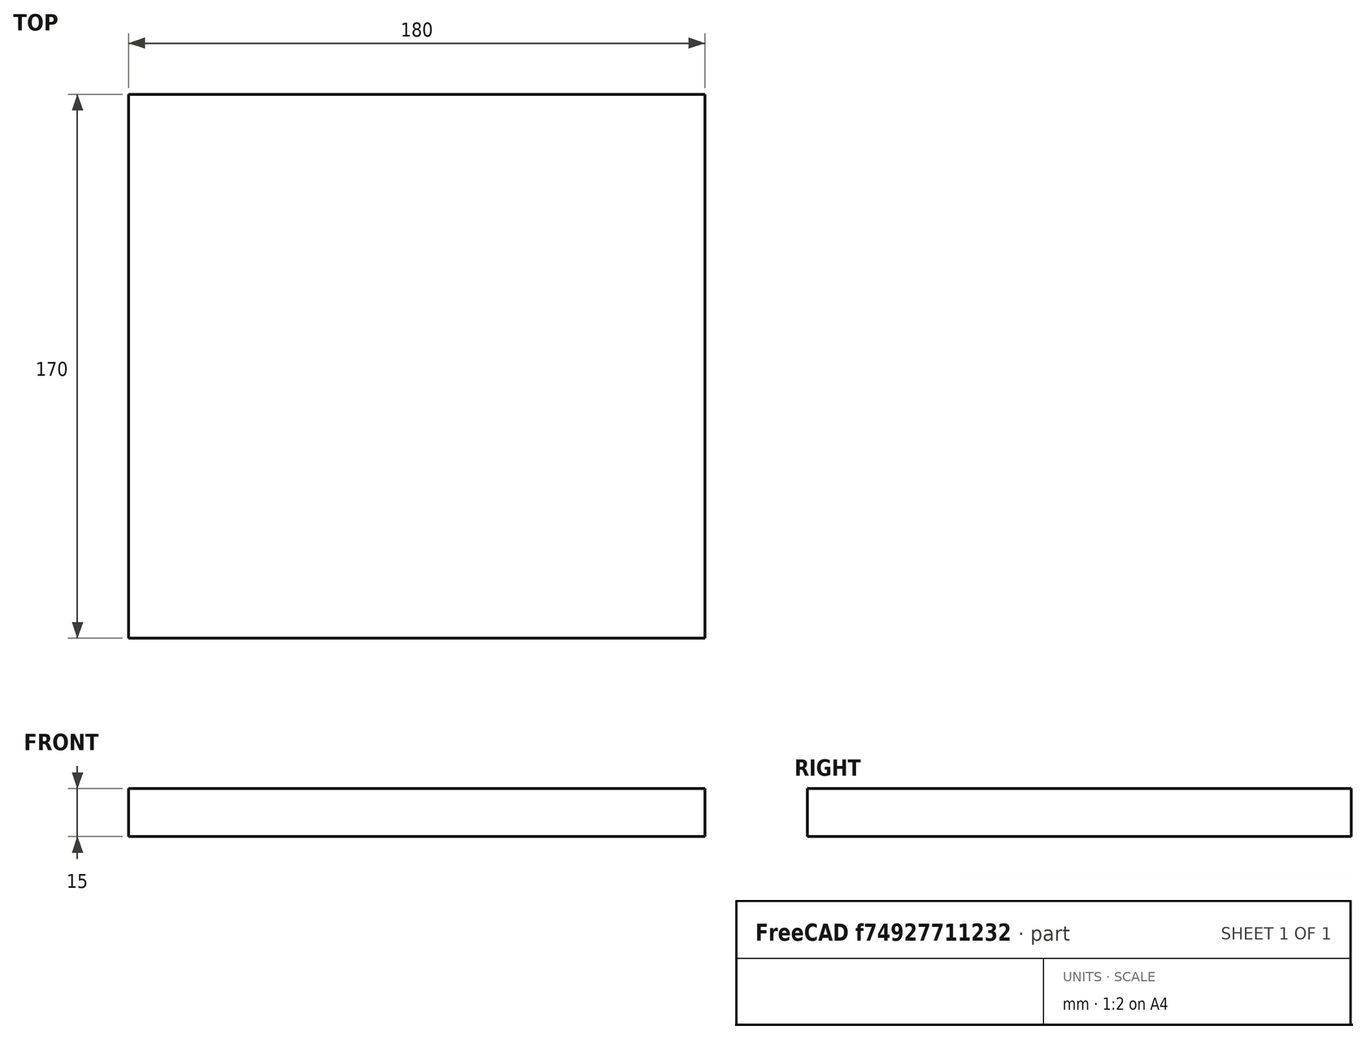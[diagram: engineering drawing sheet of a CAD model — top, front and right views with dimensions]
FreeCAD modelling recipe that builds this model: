
FCSTD DOCUMENT  (FreeCAD 0.18R4 (GitTag))
Label: MidBaseMedium
License: All rights reserved
LicenseURL: http://en.wikipedia.org/wiki/All_rights_reserved
objects: Sketcher::SketchObject×1, PartDesign::Pad×1, PartDesign::Body×1
note: 4 computed .brp shape members not serialized (recipe doc carries the construction recipe); baked Part::Feature solids carry a one-line shape summary decoded from their .brp

FEATURE [Sketcher::SketchObject] Sketch
  MapMode = 5
  Support = -> [XY_Plane]
  sketch-geometry (4):
    g0: LineSegment StartX=0 StartY=0 StartZ=0 EndX=-180 EndY=0 EndZ=0
    g1: LineSegment StartX=-180 StartY=0 StartZ=0 EndX=-180 EndY=170 EndZ=0
    g2: LineSegment StartX=-180 StartY=170 StartZ=0 EndX=0 EndY=170 EndZ=0
    g3: LineSegment StartX=0 StartY=170 StartZ=0 EndX=0 EndY=0 EndZ=0
  constraints (11):
    c: Coincident(g0,g1)
    c: Coincident(g1,g2)
    c: Coincident(g2,g3)
    c: Coincident(g3,g0)
    c: Horizontal(g0)
    c: Horizontal(g2)
    c: Vertical(g1)
    c: Vertical(g3)
    c: Distance(g2) = 180
    c: Distance(g3) = 170
    c: Coincident(g0,g-1)
FEATURE [PartDesign::Pad] Pad
  Length = 15
  Length2 = 100
  Profile = -> Sketch
  Type = 0
FEATURE [PartDesign::Body] Body
  Group = -> [Sketch,Pad]
  Origin = -> Origin
  Tip = -> Pad
